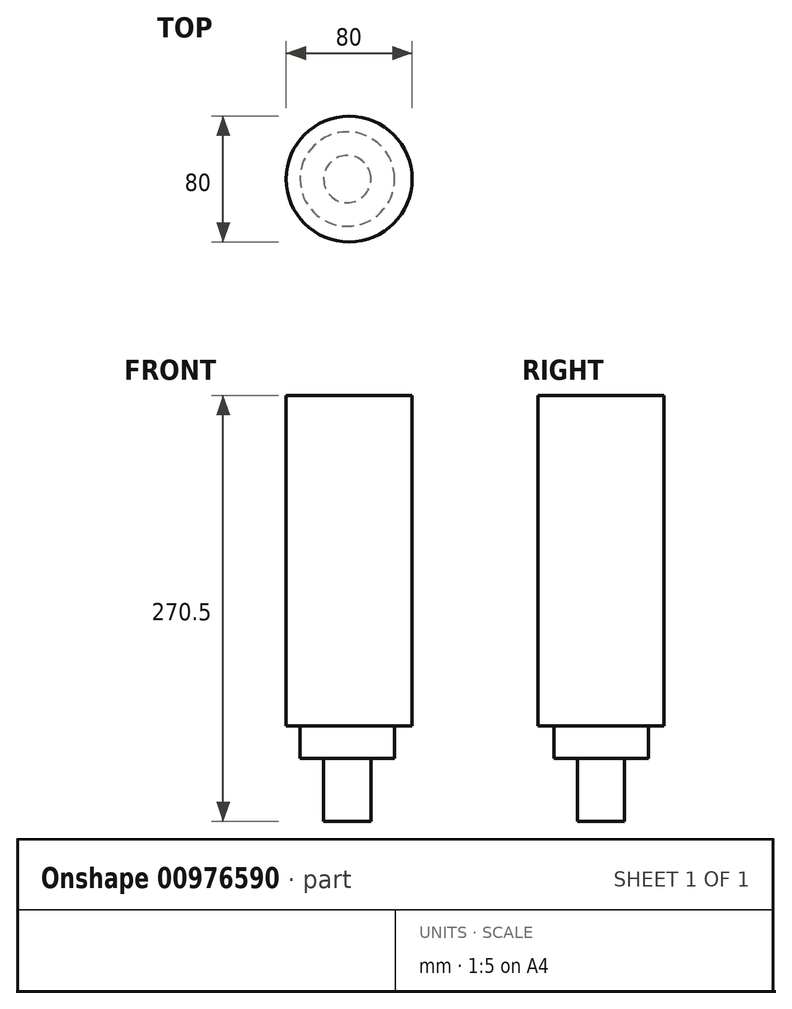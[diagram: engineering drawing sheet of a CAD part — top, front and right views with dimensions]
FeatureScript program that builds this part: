
annotation { "Feature Type Name" : "Feature", "Feature Type Description" : "" }
export const myFeature = defineFeature(function(context is Context, id is Id, definition is map)
    precondition{}
    {
        {
            var Q0;
            Q0=qCreatedBy(makeId("Top.planeOp"),FACE);
            var sketch = newSketch(context, id + "F0", { "sketchPlane" : qUnion([Q0])});
            skCircle(sketch, "E0", {"center": v(1.18, 0) * mm, "radius": 40 * mm});
            skSolve(sketch);
        }
        {
            var Q0;
            Q0 = qSketchRegion(id + "F0", true);
            extrude(context, id + "F1", {"entities" : qUnion([Q0]), "endBound" : BoundingType.SYMMETRIC, "depth" : 210 * mm, "offsetDistance" : 25 * mm});
        }
        {
            var Q0;
            Q0=makeQuery(id+"F1.opExtrude","CAP_FACE",FACE,{"disambiguationData":[OSD([sQuery(id+"F0.wireOp",EDGE,"E0")])],"isStart":true});
            var sketch = newSketch(context, id + "F2", { "sketchPlane" : qUnion([Q0])});
            skCircle(sketch, "E1", {"center": v(0, 0) * mm, "radius": 30 * mm});
            skSolve(sketch);
        }
        {
            var Q0;
            Q0 = qSketchRegion(id + "F2", true);
            extrude(context, id + "F3", {"entities" : qUnion([Q0]), "operationType" : NewBodyOperationType.ADD, "depth" : 20.5 * mm, "offsetDistance" : 25 * mm});
        }
        {
            var Q0;
            Q0=makeQuery(id+"F3.opExtrude","CAP_FACE",FACE,{"disambiguationData":[OSD([sQuery(id+"F2.wireOp",EDGE,"E1")])],"isStart":false});
            var sketch = newSketch(context, id + "F4", { "sketchPlane" : qUnion([Q0])});
            skCircle(sketch, "E2", {"center": v(0, 0) * mm, "radius": 15 * mm});
            skSolve(sketch);
        }
        {
            var Q0;
            Q0 = qSketchRegion(id + "F4", true);
            extrude(context, id + "F5", {"entities" : qUnion([Q0]), "operationType" : NewBodyOperationType.ADD, "depth" : 40 * mm, "offsetDistance" : 25 * mm});
        }
    });
